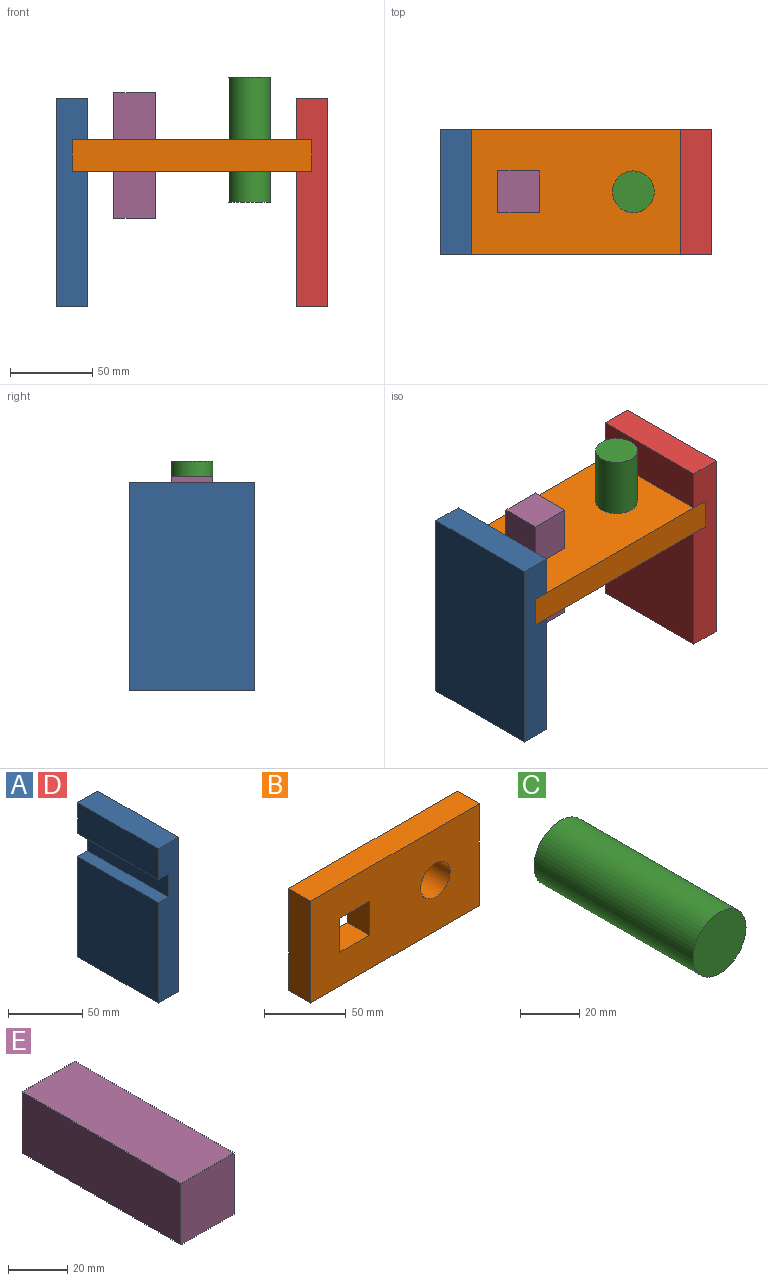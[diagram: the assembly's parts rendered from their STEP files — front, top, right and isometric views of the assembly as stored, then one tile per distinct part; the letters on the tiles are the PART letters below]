
ASSEMBLY  parts=5 mates=5
PART A: 10 faces, bbox 19.1x76.2x127 mm
  f0: plane 82.55x76.2mm, normal (-1,0,0), area 6290.3mm2, adj f1,f7,f8,f9
  f1: plane 76.2x19.05mm, normal (0,0,-1), area 1451.6mm2, adj f0,f2,f8,f9
  f2: plane 127x76.2mm, normal (1,0,0), area 9677.4mm2, adj f1,f3,f8,f9
  f3: plane 76.2x19.05mm, normal (0,0,1), area 1451.6mm2, adj f2,f4,f8,f9
  f4: plane 76.2x25.4mm, normal (-1,0,0), area 1935.5mm2, adj f3,f5,f8,f9
  f5: plane 76.2x9.53mm, normal (0,0,-1), area 725.8mm2, adj f4,f6,f8,f9
  f6: plane 76.2x19.05mm, normal (-1,0,0), area 1451.6mm2, adj f5,f7,f8,f9
  f7: plane 76.2x9.53mm, normal (0,0,1), area 725.8mm2, adj f0,f6,f8,f9
  f8: plane 127x19.05mm, normal (0,-1,0), area 2237.9mm2, adj f0,f1,f2,f3,f4,f5,f6,f7
  f9: plane 127x19.05mm, normal (0,1,0), area 2237.9mm2, adj f0,f1,f2,f3,f4,f5,f6,f7
PART B: 11 faces, bbox 146.1x19.1x76.2 mm
  f0: plane 76.2x19.05mm, normal (1,0,0), area 1451.6mm2, adj f1,f8,f9,f10
  f1: plane 146.05x19.05mm, normal (0,0,1), area 2782.3mm2, adj f0,f2,f9,f10
  f2: plane 76.2x19.05mm, normal (-1,0,0), area 1451.6mm2, adj f1,f8,f9,f10
  f3: plane 25.4x19.05mm, normal (0,0,1), area 483.9mm2, adj f4,f6,f9,f10
  f4: plane 25.4x19.05mm, normal (1,0,0), area 483.9mm2, adj f3,f5,f9,f10
  f5: plane 25.4x19.05mm, normal (0,0,-1), area 483.9mm2, adj f4,f6,f9,f10
  f6: plane 25.4x19.05mm, normal (-1,0,0), area 483.9mm2, adj f3,f5,f9,f10
  f7: cylinder r=12.7mm len=25.4mm, axis (0,1,0), area 1520.1mm2, adj f9,f10
  f8: plane 146.05x19.05mm, normal (0,0,-1), area 2782.3mm2, adj f0,f2,f9,f10
  f9: plane 146.05x76.2mm, normal (0,-1,0), area 9977.1mm2, adj f0,f1,f2,f3,f4,f5,f6,f7
  f10: plane 146.05x76.2mm, normal (0,1,0), area 9977.1mm2, adj f0,f1,f2,f3,f4,f5,f6,f7
PART C: 3 faces, bbox 25.4x76.2x25.4 mm
  f0: cylinder r=12.7mm len=76.2mm, axis (0,1,0), area 6080.5mm2, adj f1,f2
  f1: plane 25.4x25.4mm, normal (0,-1,0), area 506.7mm2, adj f0
  f2: plane 25.4x25.4mm, normal (0,1,0), area 506.7mm2, adj f0
PART D: same geometry as A
PART E: 6 faces, bbox 25.4x76.2x25.4 mm
  f0: plane 76.2x25.4mm, normal (0,0,-1), area 1935.5mm2, adj f1,f3,f4,f5
  f1: plane 76.2x25.4mm, normal (1,0,0), area 1935.5mm2, adj f0,f2,f4,f5
  f2: plane 76.2x25.4mm, normal (0,0,1), area 1935.5mm2, adj f1,f3,f4,f5
  f3: plane 76.2x25.4mm, normal (-1,0,0), area 1935.5mm2, adj f0,f2,f4,f5
  f4: plane 25.4x25.4mm, normal (0,-1,0), area 645.2mm2, adj f0,f1,f2,f3
  f5: plane 25.4x25.4mm, normal (0,1,0), area 645.2mm2, adj f0,f1,f2,f3
PLACE A rot(axis=(0,0,-1),180deg) t=(20.35,8.02,-43.35)mm
PLACE B rot(axis=(-1,0,0),90deg) t=(66.39,68.55,-27.83)mm
PLACE C rot(axis=(1,0,0),90deg) t=(128.32,64.45,29.32)mm
PLACE D t=(109.54,84.22,-43.35)mm
PLACE E rot(axis=(-0.58,0.58,-0.58),120deg) t=(2.43,50.03,-56.4)mm
MATE slider E.f0 <-> B.f4  axis (-1,0,0) through (17.32,46.12,-18.3)mm
MATE slider C.f0 <-> B.f7  axis (0,0,1) through (99.87,46.12,-8.78)mm
MATE planar B.f0 <-> D.f6  axis (1,0,0) through (137.97,46.12,-18.3)mm
MATE planar B.f2 <-> A.f6  axis (-1,0,0) through (-8.08,84.22,-18.3)mm
MATE planar A.f6 <-> B.f2  axis (1,0,0) through (-8.08,46.12,-18.3)mm
